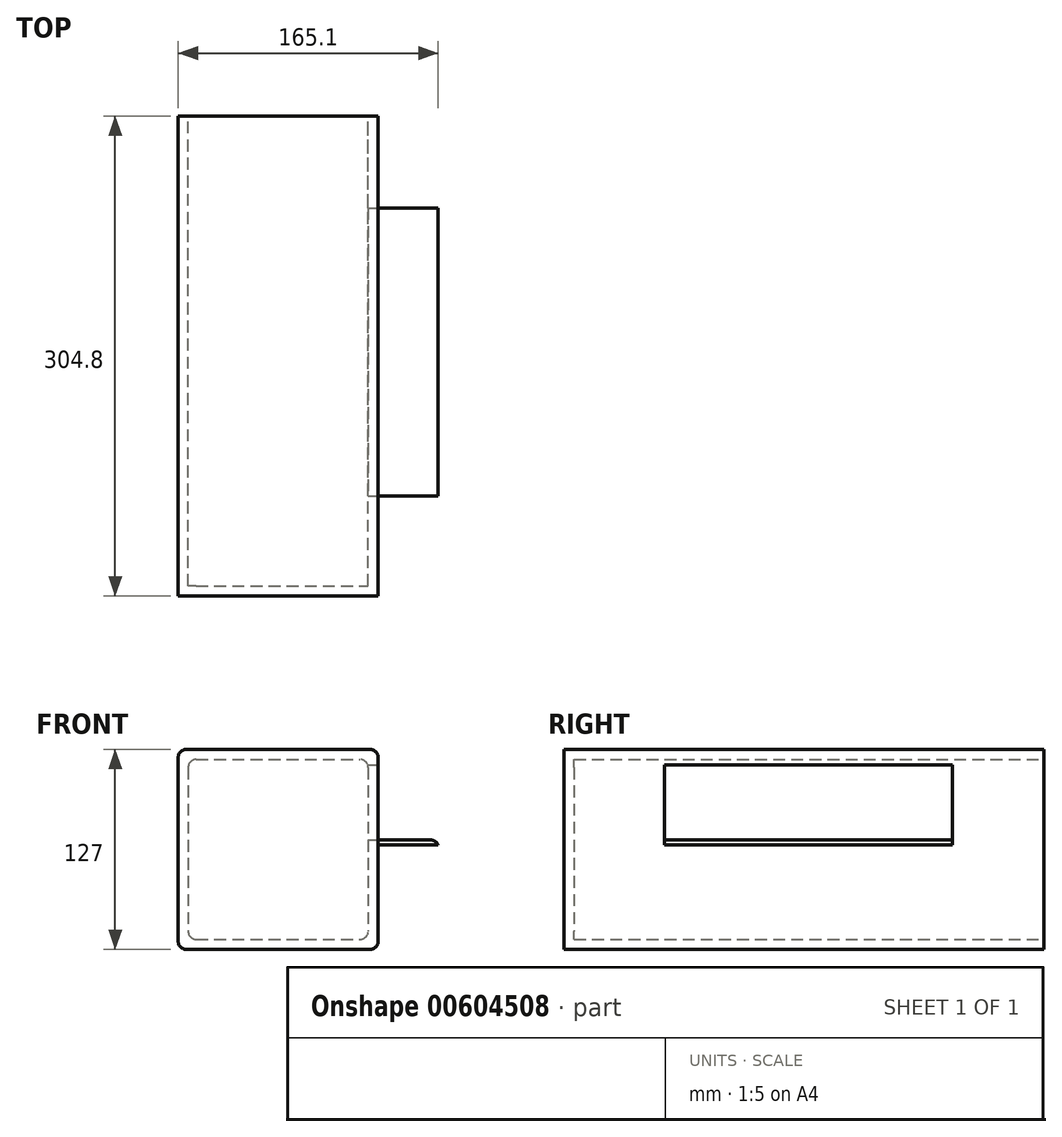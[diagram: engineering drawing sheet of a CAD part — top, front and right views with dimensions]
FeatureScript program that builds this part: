
annotation { "Feature Type Name" : "Feature", "Feature Type Description" : "" }
export const myFeature = defineFeature(function(context is Context, id is Id, definition is map)
    precondition{}
    {
        {
            var Q0;
            Q0=qCreatedBy(makeId("Front.planeOp"),FACE);
            var sketch = newSketch(context, id + "F0", { "sketchPlane" : qUnion([Q0])});
            skLineSegment(sketch, "E0.bottom", {"start": v(-63.5, 63.7) * mm, "end": v(63.5, 63.7) * mm});
            skLineSegment(sketch, "E0.top", {"start": v(-63.5, -63.3) * mm, "end": v(63.5, -63.3) * mm});
            skLineSegment(sketch, "E0.left", {"start": v(-63.5, 63.7) * mm, "end": v(-63.5, -63.3) * mm});
            skLineSegment(sketch, "E0.right", {"start": v(63.5, 63.7) * mm, "end": v(63.5, -63.3) * mm});
            skSolve(sketch);
        }
        {
            var Q0;
            Q0=makeQuery(id+"F0.imprint","IMPRINT",FACE,{"disambiguationData":[TD([[makeQuery(id+"F0.imprint","IMPRINT",EDGE,{"derivedFrom":sQuery(id+"F0.wireOp",EDGE,"E0.bottom")}),-1.0]])]});
            extrude(context, id + "F1", {"entities" : qUnion([Q0]), "oppositeDirection" : true, "depth" : 304.8 * mm, "offsetDistance" : 25.4 * mm});
        }
        {
            var Q0;
            Q0=makeQuery(id+"F1.opExtrude","SWEPT_FACE",FACE,{"disambiguationData":[OSD([sQuery(id+"F0.wireOp",EDGE,"E0.right")])]});
            var sketch = newSketch(context, id + "F2", { "sketchPlane" : qUnion([Q0])});
            skLineSegment(sketch, "E1.bottom", {"start": v(63.63, 6.17) * mm, "end": v(246.51, 6.17) * mm});
            skLineSegment(sketch, "E1.top", {"start": v(63.63, 3.12) * mm, "end": v(246.51, 3.12) * mm});
            skLineSegment(sketch, "E1.left", {"start": v(63.63, 6.17) * mm, "end": v(63.63, 3.12) * mm});
            skLineSegment(sketch, "E1.right", {"start": v(246.51, 6.17) * mm, "end": v(246.51, 3.12) * mm});
            skSolve(sketch);
        }
        {
            var Q0;
            Q0=makeQuery(id+"F2.imprint","IMPRINT",FACE,{"disambiguationData":[TD([[makeQuery(id+"F2.imprint","IMPRINT",EDGE,{"derivedFrom":sQuery(id+"F2.wireOp",EDGE,"E1.bottom")}),-1.0]])]});
            extrude(context, id + "F3", {"entities" : qUnion([Q0]), "operationType" : NewBodyOperationType.ADD, "depth" : 38.1 * mm, "offsetDistance" : 25.4 * mm});
        }
        {
            var Q0;
            Q0=makeQuery(id+"F1.opExtrude","SWEPT_FACE",FACE,{"disambiguationData":[OSD([sQuery(id+"F0.wireOp",EDGE,"E0.right")])]});
            var sketch = newSketch(context, id + "F4", { "sketchPlane" : qUnion([Q0])});
            skLineSegment(sketch, "E2.bottom", {"start": v(63.63, 6.17) * mm, "end": v(246.52, 6.17) * mm});
            skLineSegment(sketch, "E2.top", {"start": v(63.63, 53.73) * mm, "end": v(246.52, 53.73) * mm});
            skLineSegment(sketch, "E2.left", {"start": v(63.63, 6.17) * mm, "end": v(63.63, 53.73) * mm});
            skLineSegment(sketch, "E2.right", {"start": v(246.52, 6.17) * mm, "end": v(246.52, 53.73) * mm});
            skSolve(sketch);
        }
        {
            var Q0;
            Q0 = qSketchRegion(id + "F4", true);
            extrude(context, id + "F5", {"entities" : qUnion([Q0]), "operationType" : NewBodyOperationType.REMOVE, "oppositeDirection" : true, "depth" : 25.4 * mm, "offsetDistance" : 25.4 * mm});
        }
        {
            var Q0;
            Q0=makeQuery(id+"F1.opExtrude","CAP_FACE",FACE,{"disambiguationData":[OSD([sQuery(id+"F0.wireOp",EDGE,"E0.bottom"),sQuery(id+"F0.wireOp",EDGE,"E0.top"),sQuery(id+"F0.wireOp",EDGE,"E0.left"),sQuery(id+"F0.wireOp",EDGE,"E0.right")])],"isStart":false});
            var sketch = newSketch(context, id + "F6", { "sketchPlane" : qUnion([Q0])});
            skLineSegment(sketch, "E3.0", {"start": v(-57.15, 57.34) * mm, "end": v(-57.15, -56.96) * mm});
            skLineSegment(sketch, "E3.1", {"start": v(57.15, 57.34) * mm, "end": v(-57.15, 57.34) * mm});
            skLineSegment(sketch, "E3.2", {"start": v(57.15, 57.34) * mm, "end": v(57.15, -56.96) * mm});
            skLineSegment(sketch, "E3.3", {"start": v(57.15, -56.96) * mm, "end": v(-57.15, -56.96) * mm});
            skSolve(sketch);
        }
        {
            var Q0;
            Q0=makeQuery(id+"F6.imprint","IMPRINT",FACE,{"disambiguationData":[TD([[makeQuery(id+"F6.imprint","IMPRINT",EDGE,{"derivedFrom":sQuery(id+"F6.wireOp",EDGE,"E3.0")}),1.0]])]});
            extrude(context, id + "F7", {"entities" : qUnion([Q0]), "operationType" : NewBodyOperationType.REMOVE, "oppositeDirection" : true, "depth" : 298.45 * mm, "offsetDistance" : 25.4 * mm});
        }
        {
            var Q0;
            Q0=makeQuery(id+"F1.opExtrude","SWEPT_EDGE",EDGE,{"disambiguationData":[OSD([sQuery(id+"F0.wireOp",EDGE,"E0.bottom"),sQuery(id+"F0.wireOp",EDGE,"E0.left")])]});
            var Q1;
            Q1=makeQuery(id+"F1.opExtrude","SWEPT_EDGE",EDGE,{"disambiguationData":[OSD([sQuery(id+"F0.wireOp",EDGE,"E0.bottom"),sQuery(id+"F0.wireOp",EDGE,"E0.right")])]});
            var Q2;
            Q2=makeQuery(id+"F1.opExtrude","SWEPT_EDGE",EDGE,{"disambiguationData":[OSD([sQuery(id+"F0.wireOp",EDGE,"E0.top"),sQuery(id+"F0.wireOp",EDGE,"E0.right")])]});
            var Q3;
            Q3=makeQuery(id+"F1.opExtrude","SWEPT_EDGE",EDGE,{"disambiguationData":[OSD([sQuery(id+"F0.wireOp",EDGE,"E0.top"),sQuery(id+"F0.wireOp",EDGE,"E0.left")])]});
            var Q4;
            Q4=makeQuery(id+"F7.boolean.opBoolean","COPY",EDGE,{"derivedFrom":makeQuery(id+"F7.opExtrude","SWEPT_EDGE",EDGE,{"disambiguationData":[OSD([sQuery(id+"F6.wireOp",EDGE,"E3.1"),sQuery(id+"F6.wireOp",EDGE,"E3.2")])]})});
            var Q5;
            Q5=makeQuery(id+"F7.boolean.opBoolean","COPY",EDGE,{"derivedFrom":makeQuery(id+"F7.opExtrude","SWEPT_EDGE",EDGE,{"disambiguationData":[OSD([sQuery(id+"F6.wireOp",EDGE,"E3.0"),sQuery(id+"F6.wireOp",EDGE,"E3.1")])]})});
            var Q6;
            Q6=makeQuery(id+"F7.boolean.opBoolean","COPY",EDGE,{"derivedFrom":makeQuery(id+"F7.opExtrude","SWEPT_EDGE",EDGE,{"disambiguationData":[OSD([sQuery(id+"F6.wireOp",EDGE,"E3.0"),sQuery(id+"F6.wireOp",EDGE,"E3.3")])]})});
            var Q7;
            Q7=makeQuery(id+"F7.boolean.opBoolean","COPY",EDGE,{"derivedFrom":makeQuery(id+"F7.opExtrude","SWEPT_EDGE",EDGE,{"disambiguationData":[OSD([sQuery(id+"F6.wireOp",EDGE,"E3.2"),sQuery(id+"F6.wireOp",EDGE,"E3.3")])]})});
            var Q8;
            Q8=makeQuery(id+"F3.opExtrude","CAP_EDGE",EDGE,{"disambiguationData":[OSD([sQuery(id+"F2.wireOp",EDGE,"E1.bottom")])],"isStart":false});
            fillet(context, id + "F8", {"entities" : qUnion([Q0, Q1, Q2, Q3, Q4, Q5, Q6, Q7, Q8]), "radius" : 5.08 * mm, "tangentPropagation" : true, "allowEdgeOverflow" : false});
        }
    });
